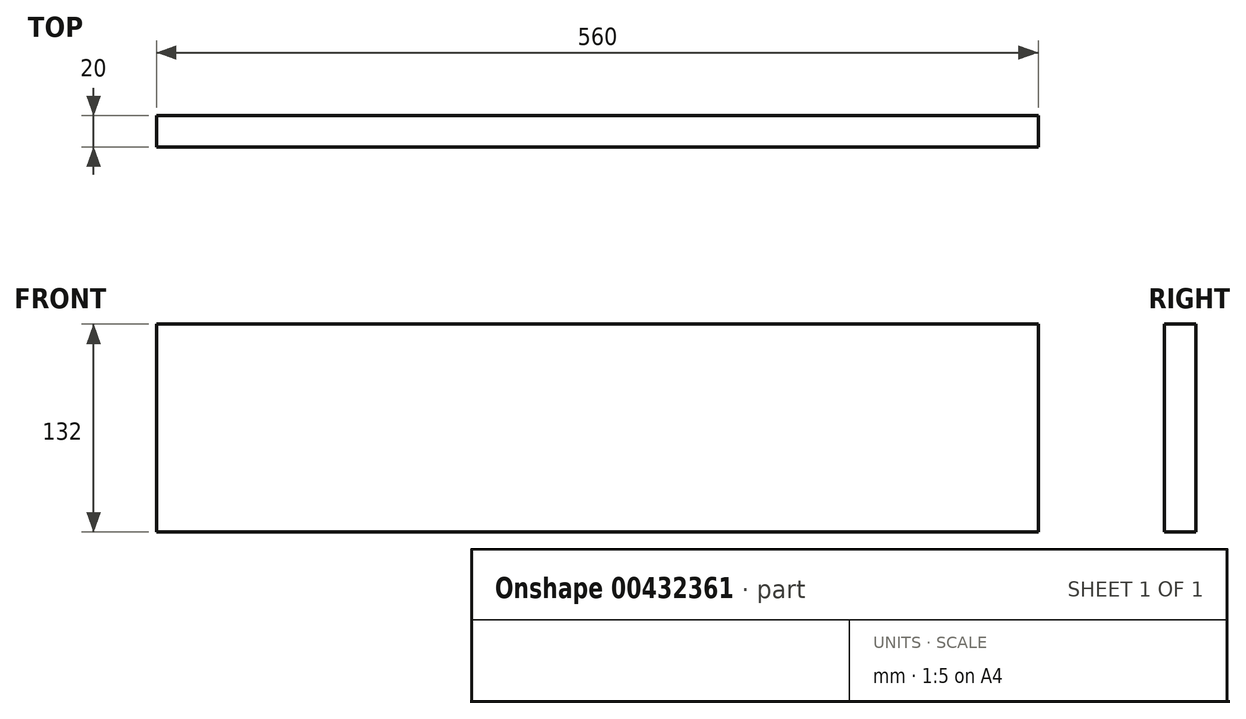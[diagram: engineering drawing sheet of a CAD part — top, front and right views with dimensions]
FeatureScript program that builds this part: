
annotation { "Feature Type Name" : "Feature", "Feature Type Description" : "" }
export const myFeature = defineFeature(function(context is Context, id is Id, definition is map)
    precondition{}
    {
        {
            var Q0;
            Q0=qCreatedBy(makeId("Front.planeOp"),FACE);
            var sketch = newSketch(context, id + "F0", { "sketchPlane" : qUnion([Q0])});
            skLineSegment(sketch, "E0.bottom", {"start": v(-280, 66) * mm, "end": v(280, 66) * mm});
            skLineSegment(sketch, "E0.top", {"start": v(-280, -66) * mm, "end": v(280, -66) * mm});
            skLineSegment(sketch, "E0.left", {"start": v(-280, 66) * mm, "end": v(-280, -66) * mm});
            skLineSegment(sketch, "E0.right", {"start": v(280, 66) * mm, "end": v(280, -66) * mm});
            skPoint(sketch, "E0.middle", {"position": v(0, 0) * mm});
            skSolve(sketch);
        }
        {
            var Q0;
            Q0 = qSketchRegion(id + "F0", true);
            extrude(context, id + "F1", {"entities" : qUnion([Q0]), "endBound" : BoundingType.SYMMETRIC, "depth" : 20 * mm});
        }
    });
